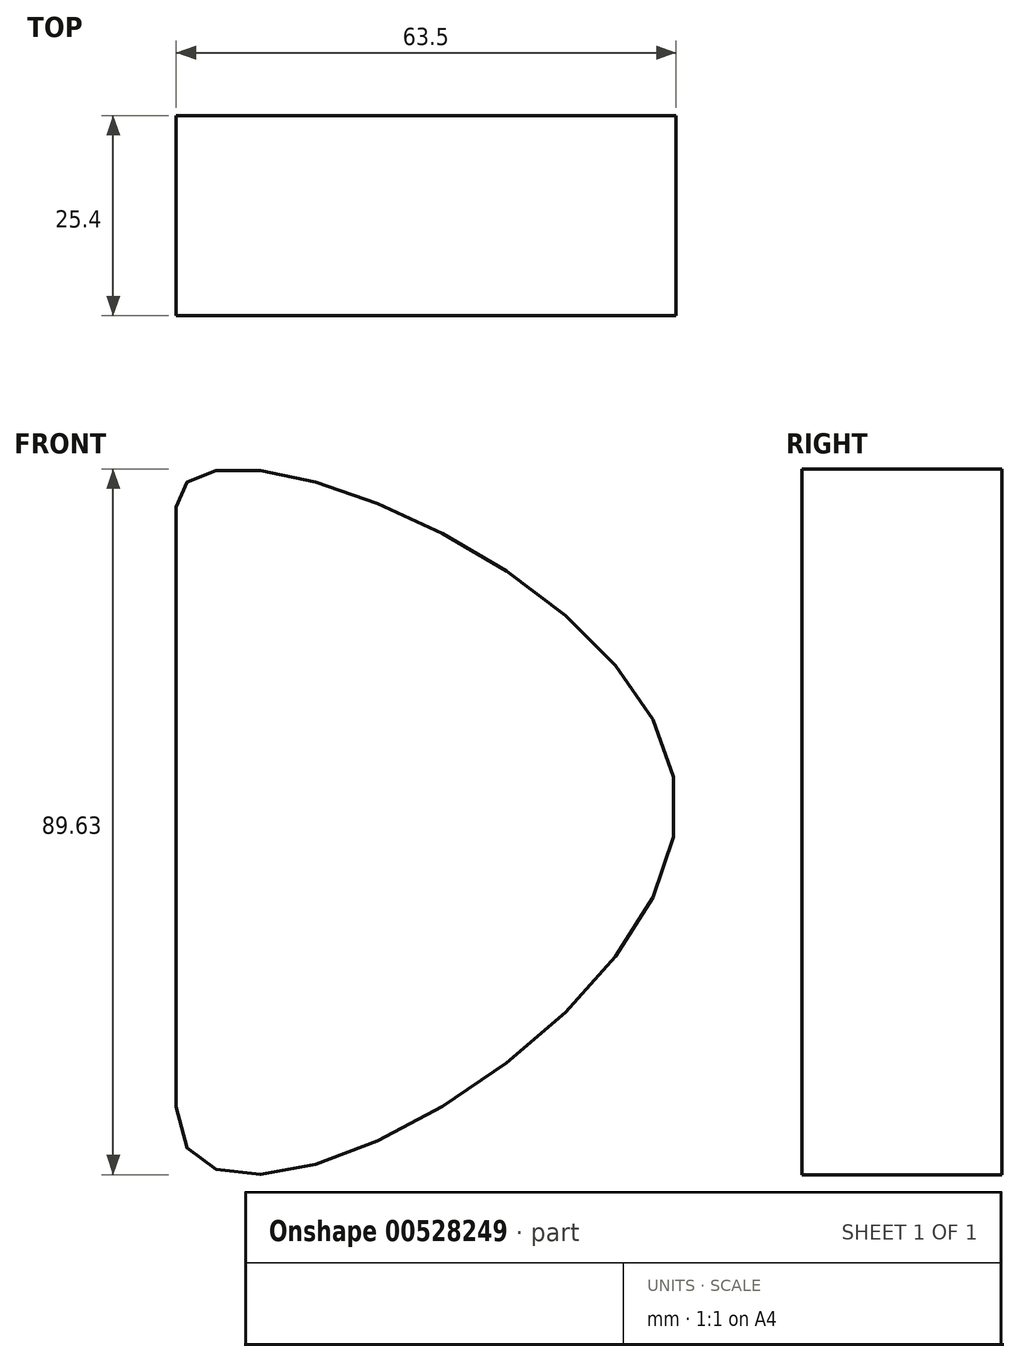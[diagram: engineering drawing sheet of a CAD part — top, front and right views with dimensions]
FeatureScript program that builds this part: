
annotation { "Feature Type Name" : "Feature", "Feature Type Description" : "" }
export const myFeature = defineFeature(function(context is Context, id is Id, definition is map)
    precondition{}
    {
        {
            var Q0;
            Q0=qCreatedBy(makeId("Front.planeOp"),FACE);
            var sketch = newSketch(context, id + "F0", { "sketchPlane" : qUnion([Q0])});
            skFitSpline(sketch, "E0", {"points": [v(0, 38.1) * mm, v(63.5, 0) * mm, v(0, -38.1) * mm], "startDerivative": vector(0, 93.06) * mm, "endDerivative": vector(0, 148.95) * mm});
            skLineSegment(sketch, "E1", {"start": v(0, -38.1) * mm, "end": v(0, 38.1) * mm});
            skSolve(sketch);
        }
        {
            var Q0;
            Q0 = qSketchRegion(id + "F0", true);
            extrude(context, id + "F1", {"entities" : qUnion([Q0]), "depth" : 25.4 * mm, "offsetDistance" : 25.4 * mm});
        }
    });
